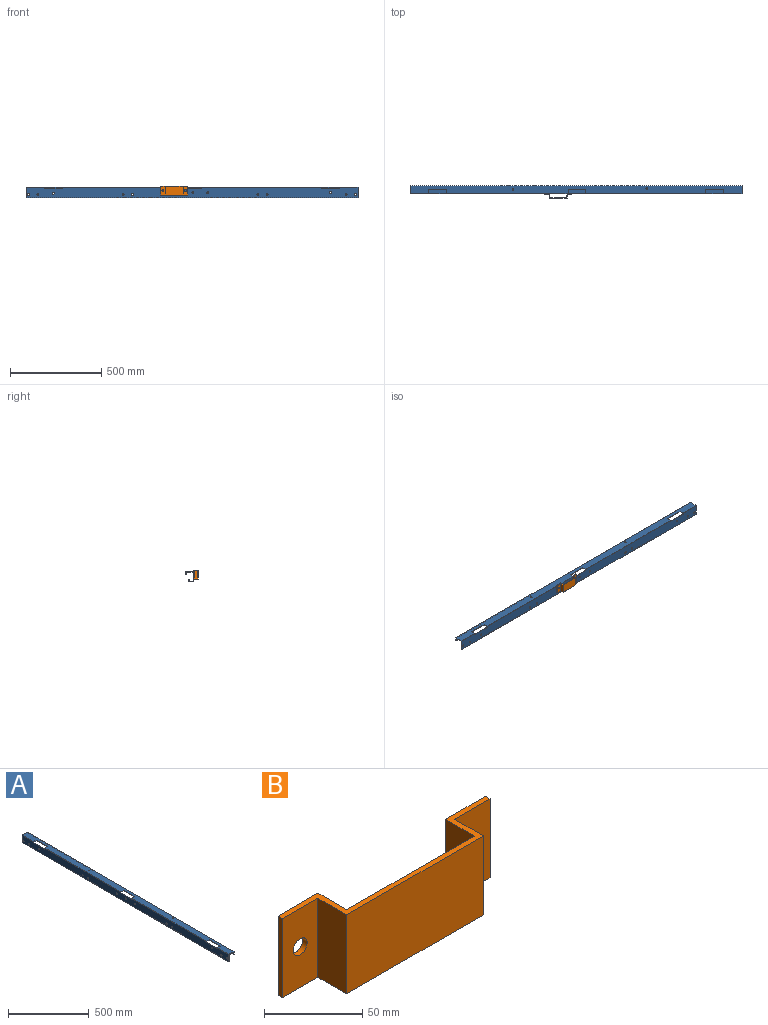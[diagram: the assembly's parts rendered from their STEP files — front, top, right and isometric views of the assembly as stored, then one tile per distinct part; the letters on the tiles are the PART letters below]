
ASSEMBLY  parts=2 mates=1
PART A: 55 faces, bbox 44.5x1816.1x57.2 mm
  f0: plane 647.7x15.88mm, normal (1,0,0), area 10282.2mm2, adj f3,f6,f51,f52
  f1: plane 393.7x15.88mm, normal (1,0,0), area 6250mm2, adj f4,f6,f50,f54
  f2: plane 428.63x15.88mm, normal (1,0,0), area 6804.4mm2, adj f5,f6,f49,f53
  f3: plane 647.7x3.3mm, normal (0,0,1), area 2138.7mm2, adj f0,f7,f51,f52
  f4: plane 393.7x3.3mm, normal (0,0,1), area 1300mm2, adj f1,f8,f50,f54
  f5: plane 428.63x3.3mm, normal (0,0,1), area 1415.3mm2, adj f2,f9,f49,f53
  f6: plane 1816.1x28.58mm, normal (0,0,-1), area 43148.7mm2, adj f0,f1,f2,f15,f19,f20,f21,f49
  f7: plane 647.7x12.57mm, normal (-1,0,0), area 8143.5mm2, adj f3,f10,f51,f52
  f8: plane 393.7x12.57mm, normal (-1,0,0), area 4950mm2, adj f4,f11,f50,f54
  f9: plane 428.63x12.57mm, normal (-1,0,0), area 5389.1mm2, adj f5,f12,f49,f53
  f10: plane 647.7x21.97mm, normal (0,0,1), area 14230.6mm2, adj f7,f15,f51,f52
  f11: plane 393.7x21.97mm, normal (0,0,1), area 8650mm2, adj f8,f15,f50,f54
  f12: plane 428.63x21.97mm, normal (0,0,1), area 9417.3mm2, adj f9,f15,f49,f53
  f13: plane 1816.1x37.85mm, normal (0,0,-1), area 62546.5mm2, adj f15,f16,f20,f21,f22,f23,f34,f35
  f14: plane 1816.1x44.45mm, normal (0,0,1), area 73580.7mm2, adj f18,f19,f20,f21,f22,f23,f34,f35
  f15: plane 1816.1x53.85mm, normal (1,0,0), area 90683mm2, adj f6,f10,f11,f12,f13,f20,f21,f24
  f16: plane 1816.1x15.75mm, normal (-1,0,0), area 28599.9mm2, adj f13,f17,f20,f21
  f17: plane 1816.1x3.3mm, normal (0,0,-1), area 5996.8mm2, adj f16,f18,f20,f21
  f18: plane 1816.1x19.05mm, normal (1,0,0), area 34596.7mm2, adj f14,f17,f20,f21
  f19: plane 1816.1x57.15mm, normal (-1,0,0), area 100574.5mm2, adj f6,f14,f20,f21,f24,f25,f26,f27
  f20: plane 57.15x44.45mm, normal (0,-1,0), area 376.6mm2, adj f6,f13,f14,f15,f16,f17,f18,f19
  f21: plane 57.15x44.45mm, normal (0,1,0), area 376.6mm2, adj f6,f13,f14,f15,f16,f17,f18,f19
  f22: cylinder r=4.97mm len=9.93mm, axis (0,0,1), area 103mm2, adj f13,f14
  f23: cylinder r=4.95mm len=9.91mm, axis (0,0,1), area 102.8mm2, adj f13,f14
  f24: cylinder r=4.95mm len=9.91mm, axis (-1,0,0), area 102.8mm2, adj f15,f19
  f25: cylinder r=4.95mm len=9.91mm, axis (-1,0,0), area 102.8mm2, adj f15,f19
  f26: cylinder r=4.95mm len=9.91mm, axis (-1,0,0), area 102.8mm2, adj f15,f19
  f27: cylinder r=4.95mm len=9.91mm, axis (-1,0,0), area 102.8mm2, adj f15,f19
  f28: cylinder r=4.95mm len=9.91mm, axis (-1,0,0), area 102.8mm2, adj f15,f19
  f29: cylinder r=4.95mm len=9.91mm, axis (-1,0,0), area 102.8mm2, adj f15,f19
  f30: cylinder r=4.95mm len=9.91mm, axis (-1,0,0), area 102.8mm2, adj f15,f19
  f31: cylinder r=4.95mm len=9.91mm, axis (-1,0,0), area 102.8mm2, adj f15,f19
  f32: cylinder r=4.95mm len=9.91mm, axis (-1,0,0), area 102.8mm2, adj f15,f19
  f33: cylinder r=4.95mm len=9.91mm, axis (-1,0,0), area 102.8mm2, adj f15,f19
  f34: plane 96.84x3.3mm, normal (-1,0,0), area 319.8mm2, adj f13,f14,f35,f36
  f35: plane 24.13x7.62mm, normal (0,1,0), area 93.9mm2, adj f13,f14,f15,f19,f34,f37
  f36: plane 24.13x7.62mm, normal (0,-1,0), area 93.9mm2, adj f13,f14,f15,f19,f34,f37
  f37: plane 96.84x3.3mm, normal (0,0,1), area 319.8mm2, adj f15,f19,f35,f36
  f38: plane 96.84x3.3mm, normal (-1,0,0), area 319.8mm2, adj f13,f14,f39,f40
  f39: plane 24.13x7.62mm, normal (0,1,0), area 93.9mm2, adj f13,f14,f15,f19,f38,f41
  f40: plane 24.13x7.62mm, normal (0,-1,0), area 93.9mm2, adj f13,f14,f15,f19,f38,f41
  f41: plane 96.84x3.3mm, normal (0,0,1), area 319.8mm2, adj f15,f19,f39,f40
  f42: plane 96.84x3.3mm, normal (-1,0,0), area 319.8mm2, adj f13,f14,f43,f44
  f43: plane 23.93x7.62mm, normal (0,-1,0), area 93.3mm2, adj f13,f14,f15,f19,f42,f45
  f44: plane 23.93x7.62mm, normal (0,1,0), area 93.3mm2, adj f13,f14,f15,f19,f42,f45
  f45: plane 96.84x3.3mm, normal (0,0,1), area 319.8mm2, adj f15,f19,f43,f44
  f46: cylinder r=4.95mm len=9.91mm, axis (-1,0,0), area 102.8mm2, adj f15,f19
  f47: cylinder r=4.95mm len=9.91mm, axis (-1,0,0), area 102.8mm2, adj f15,f19
  f48: cylinder r=4.95mm len=9.91mm, axis (-1,0,0), area 102.8mm2, adj f15,f19
  f49: plane 25.27x15.88mm, normal (0,1,0), area 125mm2, adj f2,f5,f6,f9,f12,f15
  f50: plane 25.27x15.88mm, normal (0,1,0), area 125mm2, adj f1,f4,f6,f8,f11,f15
  f51: plane 25.27x15.88mm, normal (0,-1,0), area 125mm2, adj f0,f3,f6,f7,f10,f15
  f52: plane 25.27x15.88mm, normal (0,1,0), area 125mm2, adj f0,f3,f6,f7,f10,f15
  f53: plane 25.27x15.88mm, normal (0,-1,0), area 125mm2, adj f2,f5,f6,f9,f12,f15
  f54: plane 25.27x15.88mm, normal (0,-1,0), area 125mm2, adj f1,f4,f6,f8,f11,f15
PART B: 16 faces, bbox 149.2x23.9x49.2 mm
  f0: plane 49.23x28.7mm, normal (0,1,0), area 1335.8mm2, adj f1,f11,f12,f13,f15
  f1: plane 49.23x20.78mm, normal (-1,0,0), area 1022.9mm2, adj f0,f2,f12,f13
  f2: plane 91.82x49.23mm, normal (0,1,0), area 4519.9mm2, adj f1,f3,f12,f13
  f3: plane 49.23x20.78mm, normal (1,0,0), area 1022.9mm2, adj f2,f4,f12,f13
  f4: plane 49.23x28.7mm, normal (0,1,0), area 1335.8mm2, adj f3,f5,f12,f13,f14
  f5: plane 49.23x3.3mm, normal (-1,0,0), area 162.5mm2, adj f4,f6,f12,f13
  f6: plane 49.23x25.4mm, normal (0,-1,0), area 1173.2mm2, adj f5,f7,f12,f13,f14
  f7: plane 49.23x20.62mm, normal (-1,0,0), area 1015.3mm2, adj f6,f8,f12,f13
  f8: plane 98.43x49.23mm, normal (0,-1,0), area 4845mm2, adj f7,f9,f12,f13
  f9: plane 49.23x20.62mm, normal (1,0,0), area 1015.3mm2, adj f8,f10,f12,f13
  f10: plane 49.23x25.4mm, normal (0,-1,0), area 1173.2mm2, adj f9,f11,f12,f13,f15
  f11: plane 49.23x3.3mm, normal (1,0,0), area 162.5mm2, adj f0,f10,f12,f13
  f12: plane 149.23x23.93mm, normal (0,0,1), area 614.6mm2, adj f0,f1,f2,f3,f4,f5,f6,f7
  f13: plane 149.23x23.93mm, normal (0,0,-1), area 614.6mm2, adj f0,f1,f2,f3,f4,f5,f6,f7
  f14: cylinder r=4.95mm len=9.91mm, axis (0,-1,0), area 102.8mm2, adj f4,f6
  f15: cylinder r=4.95mm len=9.91mm, axis (0,-1,0), area 102.8mm2, adj f0,f10
PLACE A rot(axis=(0,0,1),90deg) t=(0,235.66,-96.02)mm
PLACE B t=(761.5,211.73,-137.66)mm
MATE planar A.f19 <-> B.f15  axis (0,-1,0) through (907.95,235.66,-125.07)mm
